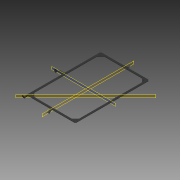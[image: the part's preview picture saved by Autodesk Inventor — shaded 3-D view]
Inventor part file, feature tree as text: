
AUTODESK INVENTOR PART (.ipt)
format: ipt  version: 2015 (Build 190159000, 159)  size: 373,248 bytes
history: native  units: mm
features: extrude x5, fillet x2, other x2, hole x1, plane x1, mirror x1
ambient origin geometry x8: Origin, YZ Plane, XZ Plane, XY Plane, X Axis, Y Axis, Z Axis, Center Point
bodies: Solid1 (feature_tree)
feature tree (12):
  extrude  "Extrusión1"  Depth=254.0mm
  extrude  "Extrusión2"  Depth=385.0mm
  fillet  "Empalme1"  Radius=10.0mm
  hole  "Agujero1"  [1 undecoded]
  extrude  "Extrusión4"  Depth=20.0mm
  plane  "Plano de trabajo1"
  extrude  "Extrusión6"  Depth=1.5mm TaperAngle=0.0deg
  extrude  "Extrusión7"  Depth=2.0mm TaperAngle=0.0deg
  mirror  "Simetría2"
  fillet  "Empalme2"  Radius=4.0mm
  other  "Eje de trabajo1"
  other  "Definición1"
note: 1 required parameter value undecoded (feature->parameter linkage not recoverable at this tier; creation-order binding heuristic only, values carry confidence <= 0.55)
